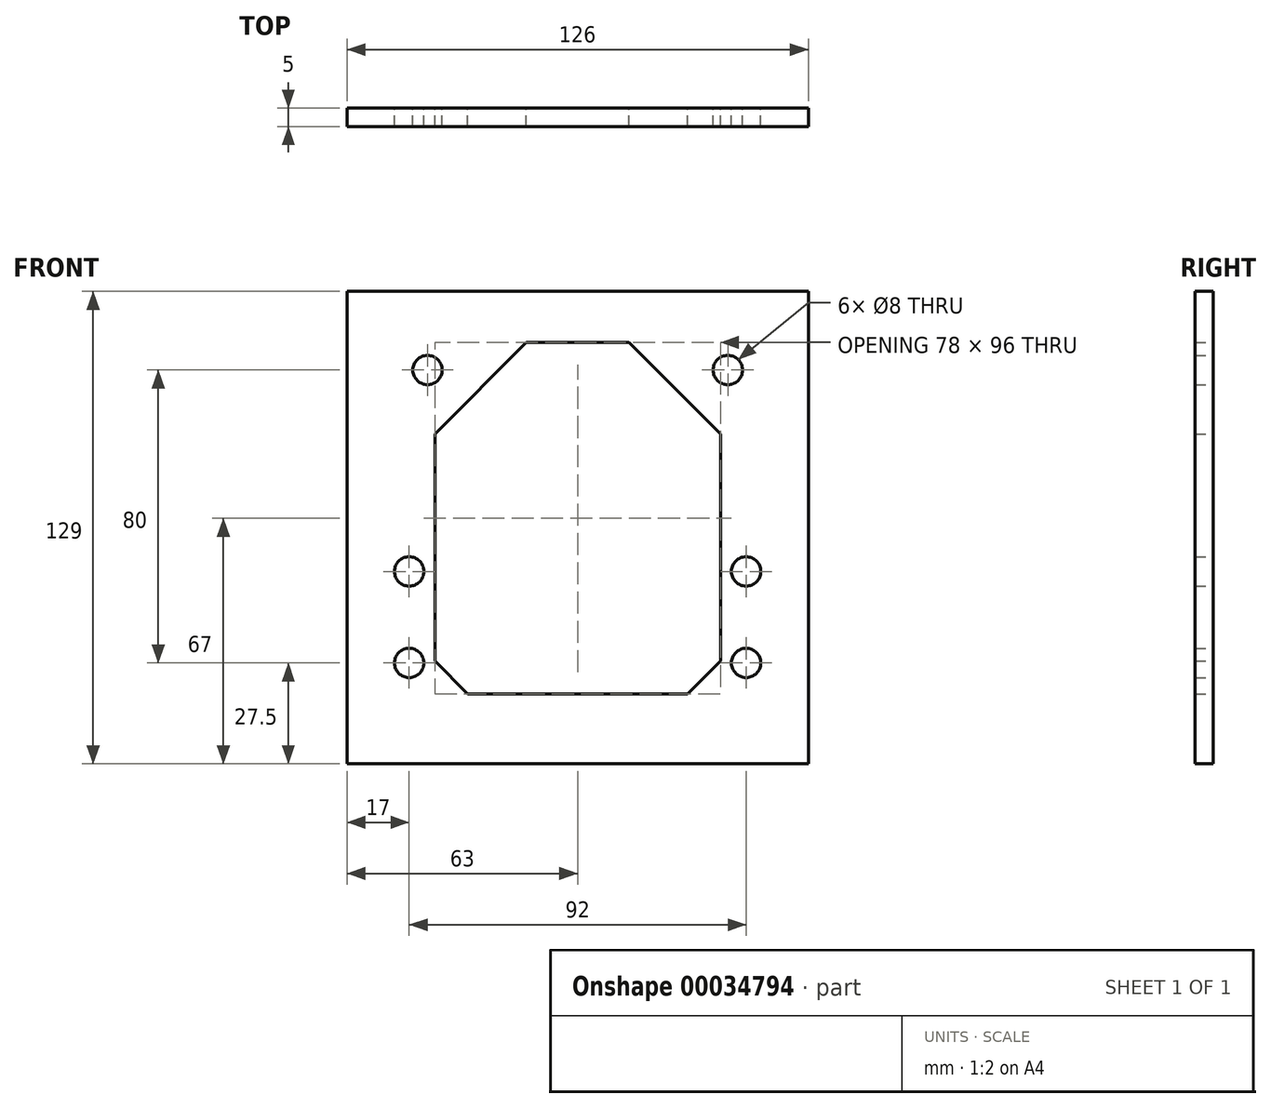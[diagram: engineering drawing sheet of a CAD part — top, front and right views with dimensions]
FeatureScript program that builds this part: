
annotation { "Feature Type Name" : "Feature", "Feature Type Description" : "" }
export const myFeature = defineFeature(function(context is Context, id is Id, definition is map)
    precondition{}
    {
        {
            var Q0;
            Q0=qCreatedBy(makeId("Front.planeOp"),FACE);
            var sketch = newSketch(context, id + "F0", { "sketchPlane" : qUnion([Q0])});
            skLineSegment(sketch, "E0.bottom", {"start": v(0, 0) * mm, "end": v(126, 0) * mm});
            skLineSegment(sketch, "E0.top", {"start": v(0, 129) * mm, "end": v(126, 129) * mm});
            skLineSegment(sketch, "E0.left", {"start": v(0, 0) * mm, "end": v(0, 129) * mm});
            skLineSegment(sketch, "E0.right", {"start": v(126, 0) * mm, "end": v(126, 129) * mm});
            skLineSegment(sketch, "E1", {"start": v(33, 19) * mm, "end": v(93, 19) * mm});
            skLineSegment(sketch, "E2", {"start": v(93, 19) * mm, "end": v(102, 28) * mm});
            skLineSegment(sketch, "E3", {"start": v(102, 28) * mm, "end": v(102, 90) * mm});
            skLineSegment(sketch, "E4", {"start": v(102, 90) * mm, "end": v(77, 115) * mm});
            skLineSegment(sketch, "E5", {"start": v(77, 115) * mm, "end": v(49, 115) * mm});
            skLineSegment(sketch, "E6", {"start": v(49, 115) * mm, "end": v(24, 90) * mm});
            skLineSegment(sketch, "E7", {"start": v(24, 90) * mm, "end": v(24, 28) * mm});
            skLineSegment(sketch, "E8", {"start": v(24, 28) * mm, "end": v(33, 19) * mm});
            skCircle(sketch, "E9", {"center": v(22, 107.5) * mm, "radius": 4 * mm});
            skCircle(sketch, "E10", {"center": v(104, 107.5) * mm, "radius": 4 * mm});
            skCircle(sketch, "E11", {"center": v(17, 52.5) * mm, "radius": 4 * mm});
            skCircle(sketch, "E12", {"center": v(17, 27.5) * mm, "radius": 4 * mm});
            skCircle(sketch, "E13", {"center": v(109, 27.5) * mm, "radius": 4 * mm});
            skCircle(sketch, "E14", {"center": v(109, 52.5) * mm, "radius": 4 * mm});
            skSolve(sketch);
        }
        {
            var Q0;
            Q0=makeQuery(id+"F0.imprint","IMPRINT",FACE,{"disambiguationData":[TD([[makeQuery(id+"F0.imprint","IMPRINT",EDGE,{"derivedFrom":sQuery(id+"F0.wireOp",EDGE,"E0.bottom")}),1.0]])]});
            extrude(context, id + "F1", {"entities" : qUnion([Q0]), "depth" : 5 * mm});
        }
    });
